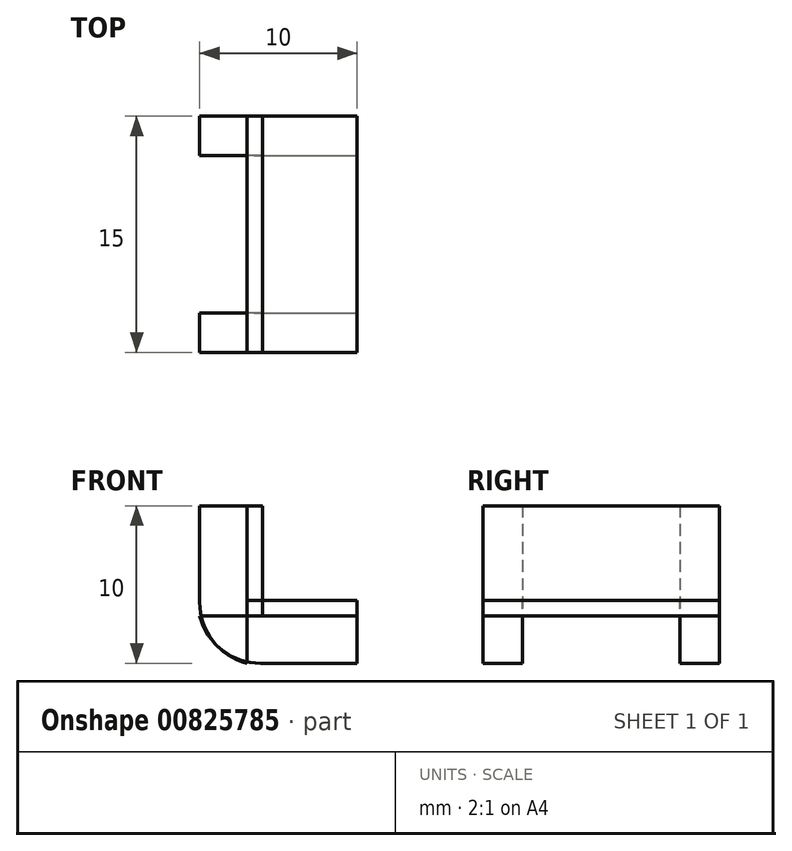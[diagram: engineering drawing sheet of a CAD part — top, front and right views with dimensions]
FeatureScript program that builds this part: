
annotation { "Feature Type Name" : "Feature", "Feature Type Description" : "" }
export const myFeature = defineFeature(function(context is Context, id is Id, definition is map)
    precondition{}
    {
        {
            var Q0;
            Q0=qCreatedBy(makeId("Top.planeOp"),FACE);
            var sketch = newSketch(context, id + "F0", { "sketchPlane" : qUnion([Q0])});
            skLineSegment(sketch, "E0.bottom", {"start": v(-5, -7.5) * mm, "end": v(5, -7.5) * mm});
            skLineSegment(sketch, "E0.top", {"start": v(-5, 7.5) * mm, "end": v(5, 7.5) * mm});
            skLineSegment(sketch, "E0.left", {"start": v(-5, -7.5) * mm, "end": v(-5, 7.5) * mm});
            skLineSegment(sketch, "E0.right", {"start": v(5, -7.5) * mm, "end": v(5, 7.5) * mm});
            skPoint(sketch, "E0.middle", {"position": v(0, 0) * mm});
            skLineSegment(sketch, "E1.bottom", {"start": v(-5, -5) * mm, "end": v(5, -5) * mm});
            skLineSegment(sketch, "E1.top", {"start": v(-5, 5) * mm, "end": v(5, 5) * mm});
            skLineSegment(sketch, "E1.left", {"start": v(-5, -5) * mm, "end": v(-5, 5) * mm});
            skLineSegment(sketch, "E1.right", {"start": v(5, -5) * mm, "end": v(5, 5) * mm});
            skLineSegment(sketch, "E2.bottom", {"start": v(-5, 7.5) * mm, "end": v(-2, 7.5) * mm});
            skLineSegment(sketch, "E2.top", {"start": v(-5, -7.5) * mm, "end": v(-2, -7.5) * mm});
            skLineSegment(sketch, "E2.left", {"start": v(-5, 7.5) * mm, "end": v(-5, -7.5) * mm});
            skLineSegment(sketch, "E2.right", {"start": v(-2, 7.5) * mm, "end": v(-2, -7.5) * mm});
            skPoint(sketch, "E2.middle", {"position": v(-3.5, 0) * mm});
            skLineSegment(sketch, "E3.bottom", {"start": v(-7, 7.5) * mm, "end": v(-5, 7.5) * mm});
            skLineSegment(sketch, "E3.top", {"start": v(-7, -7.5) * mm, "end": v(-5, -7.5) * mm});
            skLineSegment(sketch, "E3.left", {"start": v(-7, 7.5) * mm, "end": v(-7, -7.5) * mm});
            skPoint(sketch, "E3.middle", {"position": v(-6, 0) * mm});
            skSolve(sketch);
        }
        {
            var Q0;
            {var subQ0=sQuery(id+"F0.wireOp",EDGE,"E2.right");var subQ1=sQuery(id+"F0.wireOp",EDGE,"E0.bottom");var subQ2=makeQuery(id+"F0.imprint","INTERSECT",VERTEX,{"derivedFrom":[subQ1,subQ0]});Q0=makeQuery(id+"F0.imprint","IMPRINT",FACE,{"disambiguationData":[TD([[makeQuery(id+"F0.imprint","IMPRINT",EDGE,{"disambiguationData":[TD([[subQ2,-1.0]])],"derivedFrom":subQ1}),1.0]])]});}
            var Q1;
            {var subQ0=sQuery(id+"F0.wireOp",EDGE,"E2.right");var subQ1=sQuery(id+"F0.wireOp",EDGE,"E0.top");var subQ2=makeQuery(id+"F0.imprint","INTERSECT",VERTEX,{"derivedFrom":[subQ1,subQ0]});Q1=makeQuery(id+"F0.imprint","IMPRINT",FACE,{"disambiguationData":[TD([[makeQuery(id+"F0.imprint","IMPRINT",EDGE,{"disambiguationData":[TD([[subQ2,-1.0]])],"derivedFrom":subQ1}),-1.0]])]});}
            var Q2;
            {var subQ3=sQuery(id+"F0.wireOp",EDGE,"E0.left");var subQ5=sQuery(id+"F0.wireOp",EDGE,"E1.bottom");var subQ6=makeQuery(id+"F0.imprint","INTERSECT",VERTEX,{"derivedFrom":[subQ3,subQ5]});Q2=makeQuery(id+"F0.imprint","IMPRINT",FACE,{"disambiguationData":[TD([[makeQuery(id+"F0.imprint","IMPRINT",EDGE,{"disambiguationData":[TD([[subQ6,-1.0]])],"derivedFrom":subQ5}),-1.0]])]});}
            var Q3;
            {var subQ0=sQuery(id+"F0.wireOp",EDGE,"E2.right");var subQ5=sQuery(id+"F0.wireOp",EDGE,"E1.top");var subQ6=makeQuery(id+"F0.imprint","INTERSECT",VERTEX,{"derivedFrom":[subQ5,subQ0]});Q3=makeQuery(id+"F0.imprint","IMPRINT",FACE,{"disambiguationData":[TD([[makeQuery(id+"F0.imprint","IMPRINT",EDGE,{"disambiguationData":[TD([[subQ6,1.0]])],"derivedFrom":subQ5}),1.0]])]});}
            extrude(context, id + "F1", {"entities" : qUnion([Q0, Q1, Q2, Q3]), "depth" : 3 * mm, "offsetDistance" : 25 * mm});
        }
        {
            var Q0;
            {var subQ3=sQuery(id+"F0.wireOp",EDGE,"E0.left");var subQ5=sQuery(id+"F0.wireOp",EDGE,"E1.bottom");var subQ6=makeQuery(id+"F0.imprint","INTERSECT",VERTEX,{"derivedFrom":[subQ3,subQ5]});Q0=makeQuery(id+"F0.imprint","IMPRINT",FACE,{"disambiguationData":[TD([[makeQuery(id+"F0.imprint","IMPRINT",EDGE,{"disambiguationData":[TD([[subQ6,-1.0]])],"derivedFrom":subQ5}),-1.0]])]});}
            var Q1;
            {var subQ0=sQuery(id+"F0.wireOp",EDGE,"E2.right");var subQ5=sQuery(id+"F0.wireOp",EDGE,"E1.top");var subQ6=makeQuery(id+"F0.imprint","INTERSECT",VERTEX,{"derivedFrom":[subQ5,subQ0]});Q1=makeQuery(id+"F0.imprint","IMPRINT",FACE,{"disambiguationData":[TD([[makeQuery(id+"F0.imprint","IMPRINT",EDGE,{"disambiguationData":[TD([[subQ6,1.0]])],"derivedFrom":subQ5}),1.0]])]});}
            extrude(context, id + "F2", {"entities" : qUnion([Q0, Q1]), "depth" : 10 * mm, "offsetDistance" : 25 * mm});
        }
        {
            var Q0;
            Q0=makeQuery(id+"F1.opExtrude","CAP_FACE",FACE,{"disambiguationData":[OSD([sQuery(id+"F0.wireOp",EDGE,"E0.top"),sQuery(id+"F0.wireOp",EDGE,"E0.left"),sQuery(id+"F0.wireOp",EDGE,"E0.right"),sQuery(id+"F0.wireOp",EDGE,"E1.top")])],"isStart":false});
            var sketch = newSketch(context, id + "F3", { "sketchPlane" : qUnion([Q0])});
            skLineSegment(sketch, "E4.bottom", {"start": v(5, 7.5) * mm, "end": v(-2, 7.5) * mm});
            skLineSegment(sketch, "E4.top", {"start": v(5, -7.5) * mm, "end": v(-2, -7.5) * mm});
            skLineSegment(sketch, "E4.left", {"start": v(5, 7.5) * mm, "end": v(5, -7.5) * mm});
            skLineSegment(sketch, "E4.right", {"start": v(-2, 7.5) * mm, "end": v(-2, -7.5) * mm});
            skSolve(sketch);
        }
        {
            var Q0;
            Q0 = qSketchRegion(id + "F3", true);
            extrude(context, id + "F4", {"entities" : qUnion([Q0]), "depth" : 1 * mm, "offsetDistance" : 25 * mm});
        }
        {
            var Q0;
            {var subQ0=sQuery(id+"F0.wireOp",EDGE,"E2.right");Q0=makeQuery(id+"F2.opExtrude","SWEPT_FACE",FACE,{"disambiguationData":[OSD([subQ0]),TDD([makeQuery(id+"F0.imprint","IMPRINT",EDGE,{"disambiguationData":[TD([[makeQuery(id+"F0.imprint","INTERSECT",VERTEX,{"derivedFrom":[sQuery(id+"F0.wireOp",EDGE,"E0.top"),subQ0]}),-1.0]])],"derivedFrom":subQ0})])]});}
            var sketch = newSketch(context, id + "F5", { "sketchPlane" : qUnion([Q0])});
            skLineSegment(sketch, "E5.bottom", {"start": v(7.5, 3) * mm, "end": v(-7.5, 3) * mm});
            skLineSegment(sketch, "E5.top", {"start": v(7.5, 10) * mm, "end": v(-7.5, 10) * mm});
            skLineSegment(sketch, "E5.left", {"start": v(7.5, 3) * mm, "end": v(7.5, 10) * mm});
            skLineSegment(sketch, "E5.right", {"start": v(-7.5, 3) * mm, "end": v(-7.5, 10) * mm});
            skSolve(sketch);
        }
        {
            var Q0;
            Q0 = qSketchRegion(id + "F5", true);
            extrude(context, id + "F6", {"entities" : qUnion([Q0]), "depth" : 1 * mm, "offsetDistance" : 25 * mm});
        }
        {
            var Q0;
            {var subQ0=sQuery(id+"F0.wireOp",EDGE,"E0.left");Q0=makeQuery(id+"F1.opExtrude","CAP_EDGE",EDGE,{"disambiguationData":[OSD([subQ0]),TDD([makeQuery(id+"F0.imprint","IMPRINT",EDGE,{"disambiguationData":[TD([[makeQuery(id+"F0.imprint","INTERSECT",VERTEX,{"derivedFrom":[subQ0,sQuery(id+"F0.wireOp",EDGE,"E1.bottom")]}),1.0]])],"derivedFrom":subQ0})])],"isStart":true});}
            fillet(context, id + "F7", {"entities" : qUnion([Q0]), "radius" : 4 * mm, "tangentPropagation" : true, "allowEdgeOverflow" : false});
        }
        {
            var Q0;
            {var subQ0=sQuery(id+"F0.wireOp",EDGE,"E0.left");Q0=makeQuery(id+"F1.opExtrude","CAP_EDGE",EDGE,{"disambiguationData":[OSD([subQ0]),TDD([makeQuery(id+"F0.imprint","IMPRINT",EDGE,{"disambiguationData":[TD([[makeQuery(id+"F0.imprint","INTERSECT",VERTEX,{"derivedFrom":[subQ0,sQuery(id+"F0.wireOp",EDGE,"E1.top")]}),-1.0]])],"derivedFrom":subQ0})])],"isStart":true});}
            var Q1;
            {var subQ0=sQuery(id+"F0.wireOp",EDGE,"E0.left");Q1=makeQuery(id+"F2.opExtrude","CAP_EDGE",EDGE,{"disambiguationData":[OSD([subQ0]),TDD([makeQuery(id+"F0.imprint","IMPRINT",EDGE,{"disambiguationData":[TD([[makeQuery(id+"F0.imprint","INTERSECT",VERTEX,{"derivedFrom":[subQ0,sQuery(id+"F0.wireOp",EDGE,"E1.bottom")]}),1.0]])],"derivedFrom":subQ0})])],"isStart":true});}
            fillet(context, id + "F8", {"entities" : qUnion([Q0, Q1]), "radius" : 4 * mm, "tangentPropagation" : true, "allowEdgeOverflow" : false});
        }
        {
            var Q0;
            {var subQ0=sQuery(id+"F0.wireOp",EDGE,"E0.left");Q0=makeQuery(id+"F2.opExtrude","CAP_EDGE",EDGE,{"disambiguationData":[OSD([subQ0]),TDD([makeQuery(id+"F0.imprint","IMPRINT",EDGE,{"disambiguationData":[TD([[makeQuery(id+"F0.imprint","INTERSECT",VERTEX,{"derivedFrom":[subQ0,sQuery(id+"F0.wireOp",EDGE,"E1.top")]}),-1.0]])],"derivedFrom":subQ0})])],"isStart":true});}
            fillet(context, id + "F9", {"entities" : qUnion([Q0]), "radius" : 4 * mm, "tangentPropagation" : true, "allowEdgeOverflow" : false});
        }
    });
